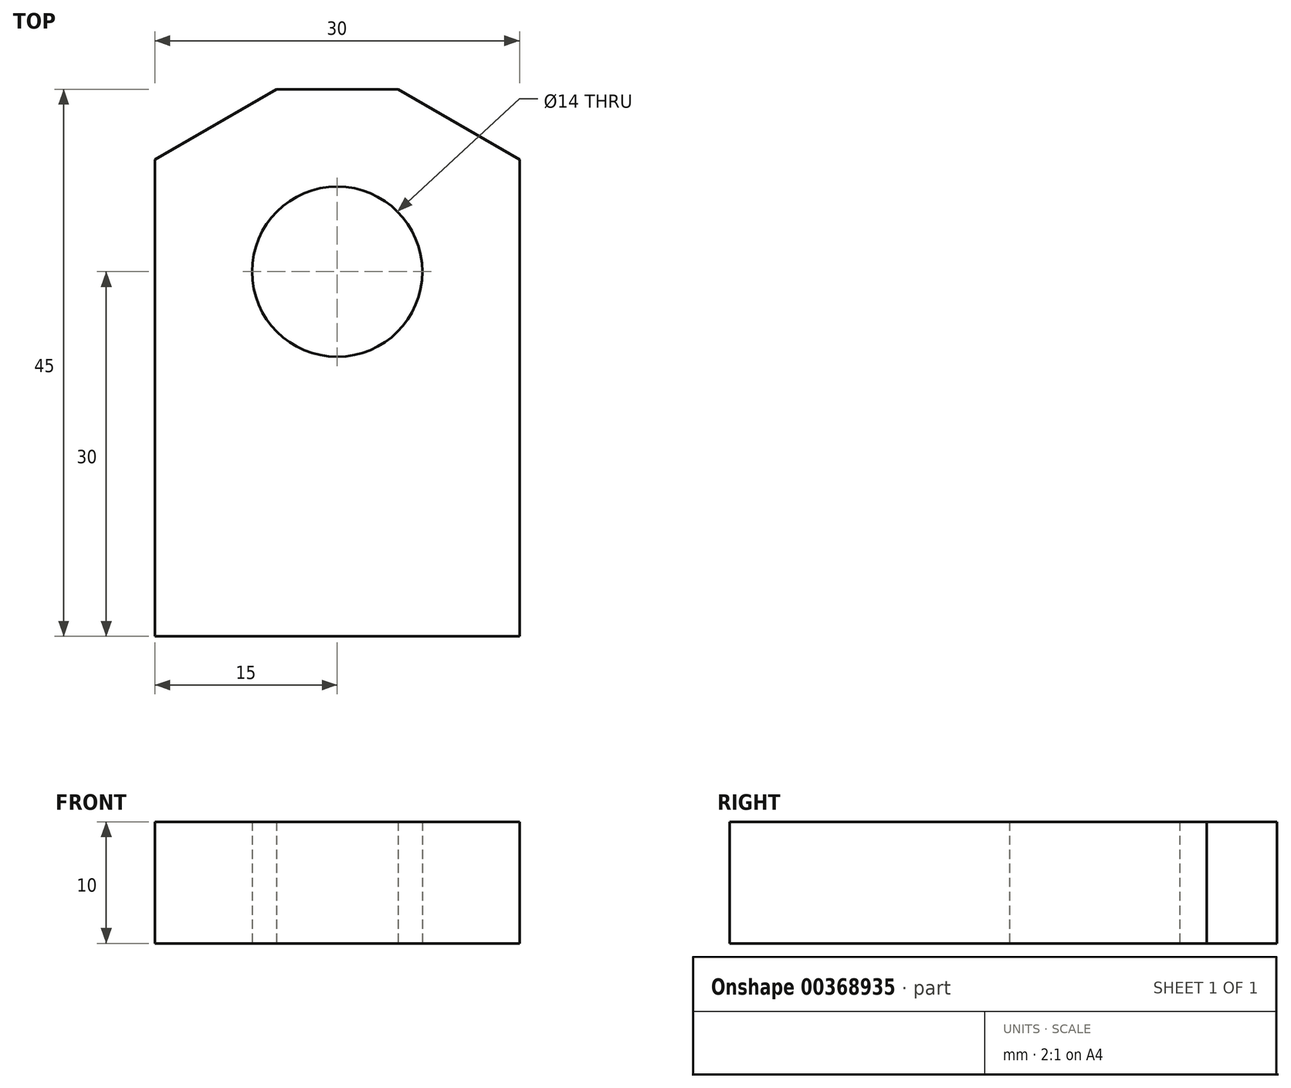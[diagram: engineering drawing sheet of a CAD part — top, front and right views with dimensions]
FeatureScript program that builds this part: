
annotation { "Feature Type Name" : "Feature", "Feature Type Description" : "" }
export const myFeature = defineFeature(function(context is Context, id is Id, definition is map)
    precondition{}
    {
        {
            var Q0;
            Q0=qCreatedBy(makeId("Top.planeOp"),FACE);
            var sketch = newSketch(context, id + "F0", { "sketchPlane" : qUnion([Q0])});
            skLineSegment(sketch, "E0.bottom", {"start": v(0, 0) * mm, "end": v(30, 0) * mm});
            skLineSegment(sketch, "E0.top", {"start": v(10, 45) * mm, "end": v(20, 45) * mm});
            skLineSegment(sketch, "E0.left", {"start": v(0, 0) * mm, "end": v(0, 39.23) * mm});
            skLineSegment(sketch, "E0.right", {"start": v(30, 0) * mm, "end": v(30, 39.23) * mm});
            skLineSegment(sketch, "E1", {"start": v(10, 45) * mm, "end": v(0, 39.23) * mm});
            skLineSegment(sketch, "E2", {"start": v(30, 39.23) * mm, "end": v(20, 45) * mm});
            skCircle(sketch, "E3", {"center": v(15, 30) * mm, "radius": 7 * mm});
            skPoint(sketch, "E3.centerSnap0", {"position": v(15, 45) * mm});
            skPoint(sketch, "E4.orphan", {"position": v(0, 45) * mm});
            skPoint(sketch, "E5.orphan", {"position": v(30, 45) * mm});
            skSolve(sketch);
        }
        {
            var Q0;
            Q0 = qSketchRegion(id + "F0", true);
            extrude(context, id + "F1", {"entities" : qUnion([Q0]), "depth" : 10 * mm});
        }
    });
